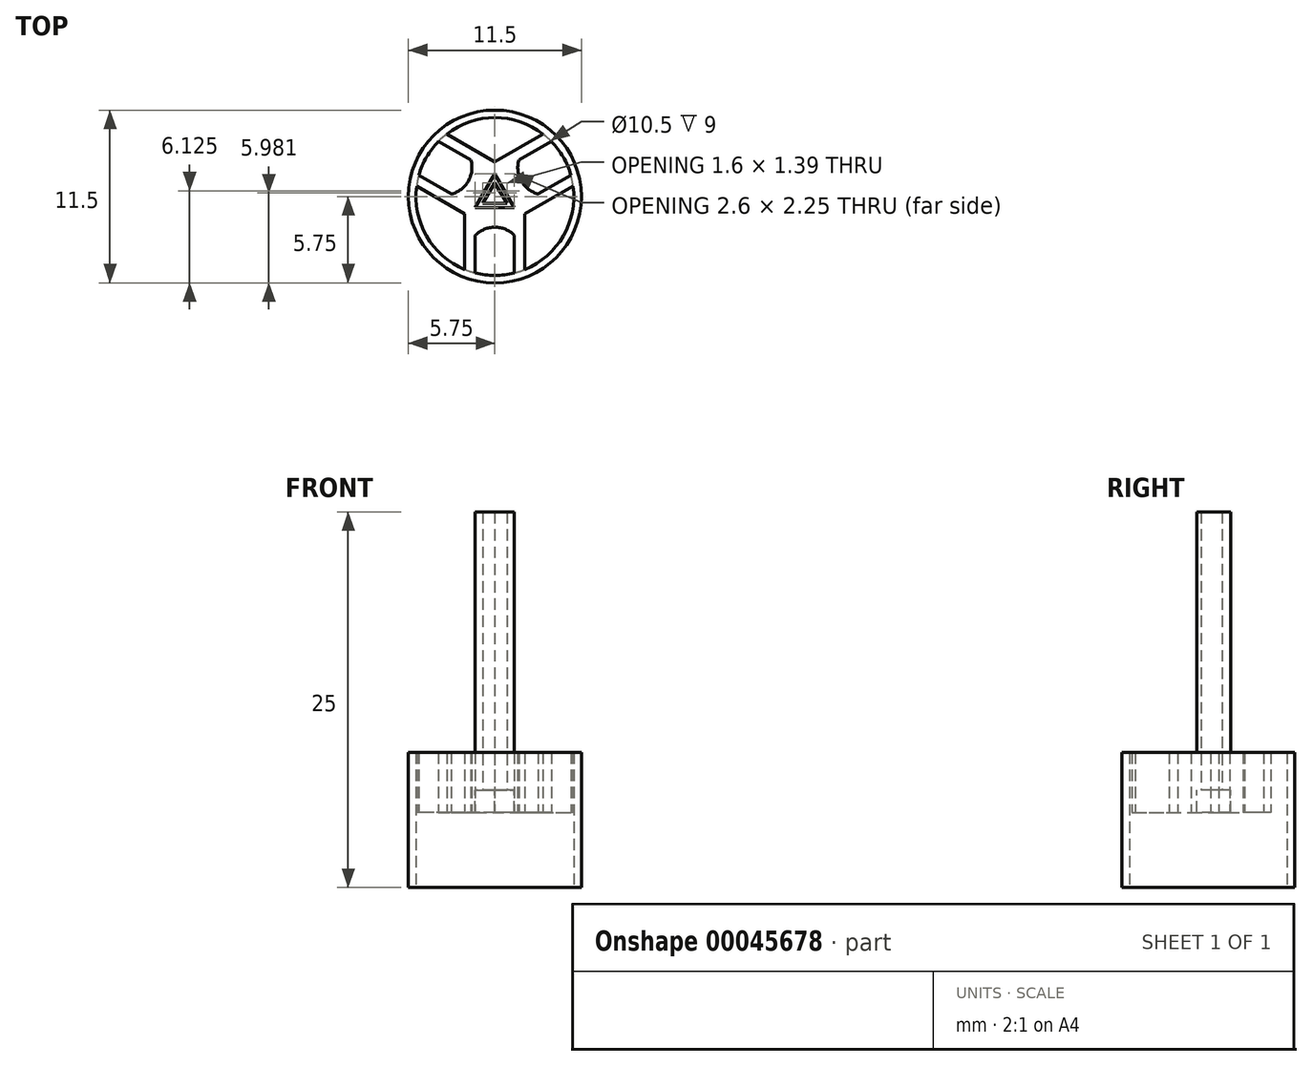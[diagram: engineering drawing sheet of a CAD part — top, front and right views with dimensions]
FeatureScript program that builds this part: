
annotation { "Feature Type Name" : "Feature", "Feature Type Description" : "" }
export const myFeature = defineFeature(function(context is Context, id is Id, definition is map)
    precondition{}
    {
        {
            var Q0;
            Q0=qCreatedBy(makeId("Top.planeOp"),FACE);
            var sketch = newSketch(context, id + "F0", { "sketchPlane" : qUnion([Q0])});
            skCircle(sketch, "E0", {"center": v(0, 0) * mm, "radius": 5.25 * mm});
            skCircle(sketch, "E1", {"center": v(0, 0) * mm, "radius": 5.75 * mm});
            skLineSegment(sketch, "E2", {"start": v(0, 5.25) * mm, "end": v(0, 0) * mm, "construction": true});
            skLineSegment(sketch, "E3", {"start": v(0, 0) * mm, "end": v(-4.55, -2.62) * mm, "construction": true});
            skLineSegment(sketch, "E4", {"start": v(0, 0) * mm, "end": v(4.55, -2.62) * mm, "construction": true});
            skLineSegment(sketch, "E5", {"start": v(0, 0.92) * mm, "end": v(-0.8, -0.46) * mm});
            skLineSegment(sketch, "E6", {"start": v(-0.8, -0.46) * mm, "end": v(0.8, -0.46) * mm});
            skLineSegment(sketch, "E7", {"start": v(0.8, -0.46) * mm, "end": v(0, 0.92) * mm});
            skLineSegment(sketch, "E8", {"start": v(0, 1.5) * mm, "end": v(-1.3, -0.75) * mm});
            skLineSegment(sketch, "E9", {"start": v(-1.3, -0.75) * mm, "end": v(1.3, -0.75) * mm});
            skLineSegment(sketch, "E10", {"start": v(1.3, -0.75) * mm, "end": v(0, 1.5) * mm});
            skLineSegment(sketch, "E11", {"start": v(0, 0) * mm, "end": v(4.55, 2.62) * mm, "construction": true});
            skLineSegment(sketch, "E12", {"start": v(0, 0) * mm, "end": v(0, -5.25) * mm, "construction": true});
            skLineSegment(sketch, "E13", {"start": v(0, 0) * mm, "end": v(-4.55, 2.63) * mm, "construction": true});
            skLineSegment(sketch, "E14", {"start": v(3.76, 3.67) * mm, "end": v(1.59, 2.42) * mm});
            skLineSegment(sketch, "E15", {"start": v(2.89, 0.17) * mm, "end": v(5.06, 1.42) * mm});
            skLineSegment(sketch, "E16", {"start": v(-1.3, -5.09) * mm, "end": v(-1.3, -2.59) * mm});
            skLineSegment(sketch, "E17", {"start": v(1.3, -2.59) * mm, "end": v(1.3, -5.09) * mm});
            skLineSegment(sketch, "E18", {"start": v(-3.76, 3.67) * mm, "end": v(-1.59, 2.42) * mm});
            skLineSegment(sketch, "E19", {"start": v(-2.89, 0.17) * mm, "end": v(-5.06, 1.42) * mm});
            skArc(sketch, "E20", {"start": v(1.59, 2.42) * mm, "mid": v(1.77, 1.02) * mm, "end": v(2.89, 0.17) * mm});
            skArc(sketch, "E21", {"start": v(1.3, -2.59) * mm, "mid": v(0, -2.04) * mm, "end": v(-1.3, -2.59) * mm});
            skArc(sketch, "E22", {"start": v(-2.89, 0.17) * mm, "mid": v(-1.77, 1.02) * mm, "end": v(-1.59, 2.42) * mm});
            skLineSegment(sketch, "E23", {"start": v(3.2, 4.16) * mm, "end": v(0, 2.3) * mm});
            skLineSegment(sketch, "E24", {"start": v(0, 2.3) * mm, "end": v(-3.2, 4.16) * mm});
            skLineSegment(sketch, "E25", {"start": v(2, -4.85) * mm, "end": v(2, -1.15) * mm});
            skLineSegment(sketch, "E26", {"start": v(2, -1.15) * mm, "end": v(5.2, 0.7) * mm});
            skLineSegment(sketch, "E27", {"start": v(-2, -4.85) * mm, "end": v(-2, -1.15) * mm});
            skLineSegment(sketch, "E28", {"start": v(-2, -1.15) * mm, "end": v(-5.2, 0.7) * mm});
            skSolve(sketch);
        }
        {
            var Q0;
            Q0=makeQuery(id+"F0.imprint","IMPRINT",FACE,{"disambiguationData":[TD([[makeQuery(id+"F0.imprint","IMPRINT",EDGE,{"derivedFrom":sQuery(id+"F0.wireOp",EDGE,"E8")}),-1.0]])]});
            var Q1;
            Q1=makeQuery(id+"F0.imprint","IMPRINT",FACE,{"disambiguationData":[TD([[makeQuery(id+"F0.imprint","IMPRINT",EDGE,{"derivedFrom":sQuery(id+"F0.wireOp",EDGE,"E1")}),1.0]])]});
            extrude(context, id + "F1", {"entities" : qUnion([Q0, Q1]), "depth" : 2.5 * mm});
        }
        {
            var Q0;
            Q0=makeQuery(id+"F0.imprint","IMPRINT",FACE,{"disambiguationData":[TD([[makeQuery(id+"F0.imprint","IMPRINT",EDGE,{"derivedFrom":sQuery(id+"F0.wireOp",EDGE,"E5")}),-1.0]])]});
            extrude(context, id + "F2", {"entities" : qUnion([Q0]), "operationType" : NewBodyOperationType.ADD, "depth" : 18.5 * mm});
        }
        {
            var Q0;
            Q0=makeQuery(id+"F0.imprint","IMPRINT",FACE,{"disambiguationData":[TD([[makeQuery(id+"F0.imprint","IMPRINT",EDGE,{"derivedFrom":sQuery(id+"F0.wireOp",EDGE,"E1")}),1.0]])]});
            extrude(context, id + "F3", {"entities" : qUnion([Q0]), "operationType" : NewBodyOperationType.ADD, "oppositeDirection" : true, "depth" : 6.5 * mm});
        }
        {
            var Q0;
            Q0=makeQuery(id+"F0.imprint","IMPRINT",FACE,{"disambiguationData":[TD([[makeQuery(id+"F0.imprint","IMPRINT",EDGE,{"derivedFrom":sQuery(id+"F0.wireOp",EDGE,"E8")}),-1.0]])]});
            extrude(context, id + "F4", {"entities" : qUnion([Q0]), "operationType" : NewBodyOperationType.ADD, "oppositeDirection" : true, "depth" : 1.5 * mm});
        }
    });
